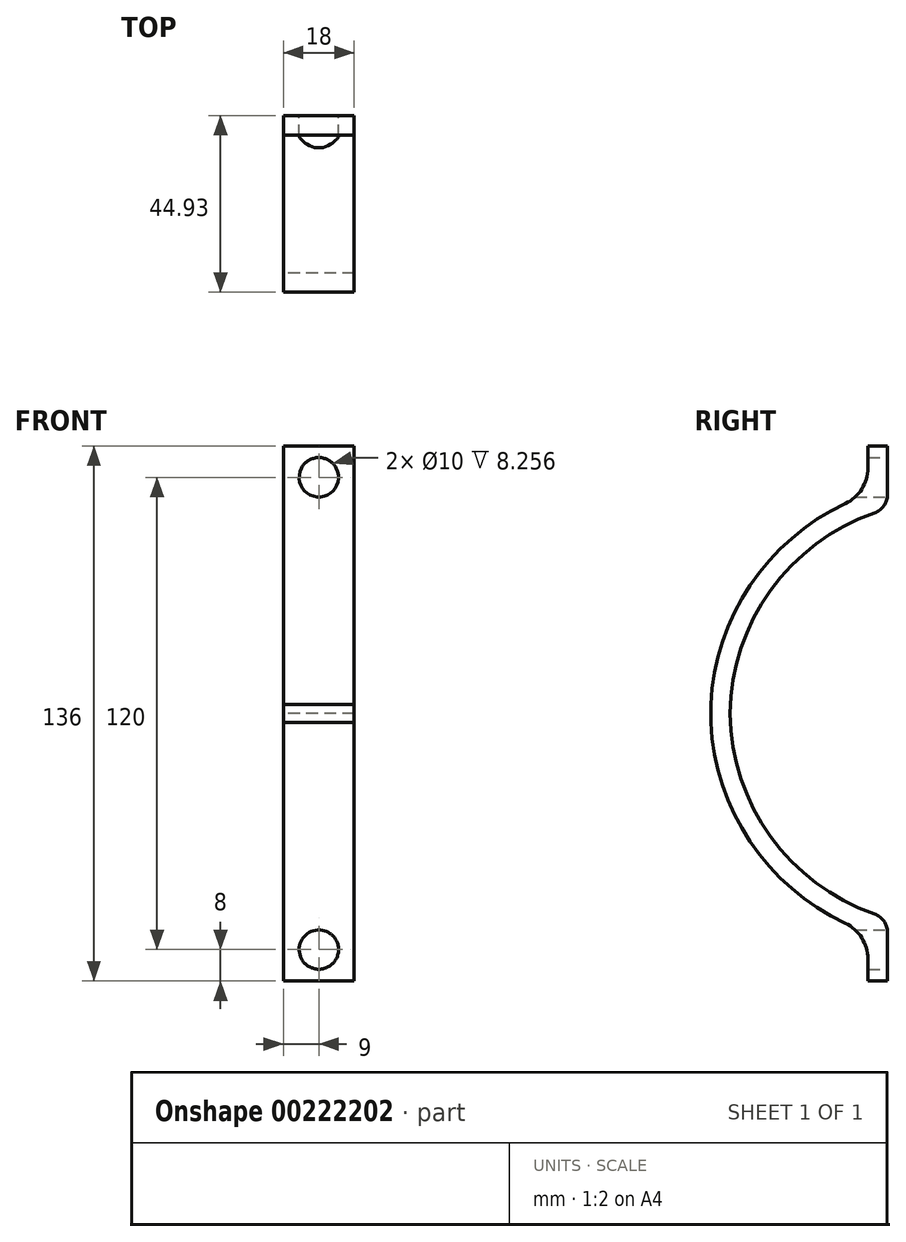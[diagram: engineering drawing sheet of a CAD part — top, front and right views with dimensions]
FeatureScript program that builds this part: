
annotation { "Feature Type Name" : "Feature", "Feature Type Description" : "" }
export const myFeature = defineFeature(function(context is Context, id is Id, definition is map)
    precondition{}
    {
        {
            var Q0;
            Q0=qCreatedBy(makeId("Right.planeOp"),FACE);
            var sketch = newSketch(context, id + "F0", { "sketchPlane" : qUnion([Q0])});
            skLineSegment(sketch, "E0", {"start": v(0, 68) * mm, "end": v(0, 55.67) * mm});
            skLineSegment(sketch, "E1", {"start": v(0, 0) * mm, "end": v(-40, 0) * mm});
            skArc(sketch, "E2", {"start": v(-3.35, 50.95) * mm, "mid": v(-29.72, 31.26) * mm, "end": v(-40, 0) * mm});
            skLineSegment(sketch, "E3", {"start": v(0, 68) * mm, "end": v(-5, 68) * mm});
            skLineSegment(sketch, "E4", {"start": v(-5, 68) * mm, "end": v(-5, 62.37) * mm});
            skArc(sketch, "E5.0", {"start": v(-10.74, 53.33) * mm, "mid": v(-34.92, 32.53) * mm, "end": v(-44.93, 2.26) * mm});
            skLineSegment(sketch, "E6", {"start": v(-44.93, 2.26) * mm, "end": v(-44.93, 0) * mm});
            skLineSegment(sketch, "E7", {"start": v(-44.93, 0) * mm, "end": v(-40, 0) * mm});
            skPoint(sketch, "E8.orphan", {"position": v(0, 57.17) * mm});
            skPoint(sketch, "E9.visualSharp", {"position": v(-5, 55.67) * mm});
            skArc(sketch, "E9.filletArc", {"start": v(-10.74, 53.33) * mm, "mid": v(-6.56, 57.02) * mm, "end": v(-5, 62.37) * mm});
            skPoint(sketch, "E10.visualSharp", {"position": v(0, 52) * mm});
            skArc(sketch, "E10.filletArc", {"start": v(-3.35, 50.95) * mm, "mid": v(-0.92, 52.78) * mm, "end": v(0, 55.67) * mm});
            skLineSegment(sketch, "E11.MirrorCS", {"start": v(-5, -68) * mm, "end": v(-5, -62.37) * mm});
            skArc(sketch, "E12.MirrorCS", {"start": v(-3.35, -50.95) * mm, "mid": v(-0.92, -52.78) * mm, "end": v(0, -55.67) * mm});
            skPoint(sketch, "E13.MirrorP", {"position": v(0, -57.17) * mm});
            skArc(sketch, "E14.MirrorCS", {"start": v(-3.35, -50.95) * mm, "mid": v(-29.72, -31.26) * mm, "end": v(-40, 0) * mm});
            skPoint(sketch, "E15.MirrorP", {"position": v(0, -52) * mm});
            skArc(sketch, "E16.MirrorCS", {"start": v(-10.74, -53.33) * mm, "mid": v(-6.56, -57.02) * mm, "end": v(-5, -62.37) * mm});
            skArc(sketch, "E17.MirrorCS", {"start": v(-10.74, -53.33) * mm, "mid": v(-34.92, -32.53) * mm, "end": v(-44.93, -2.26) * mm});
            skLineSegment(sketch, "E18.MirrorCS", {"start": v(0, -68) * mm, "end": v(0, -55.67) * mm});
            skLineSegment(sketch, "E19.MirrorCS", {"start": v(-44.93, -2.26) * mm, "end": v(-44.93, 0) * mm});
            skLineSegment(sketch, "E20.MirrorCS", {"start": v(0, -68) * mm, "end": v(-5, -68) * mm});
            skPoint(sketch, "E21", {"position": v(-2.74, 60) * mm});
            skPoint(sketch, "E22.MirrorP", {"position": v(-2.74, -60) * mm});
            skSolve(sketch);
        }
        {
            var Q0;
            Q0=makeQuery(id+"F0.imprint","IMPRINT",FACE,{"disambiguationData":[TD([[makeQuery(id+"F0.imprint","IMPRINT",EDGE,{"derivedFrom":sQuery(id+"F0.wireOp",EDGE,"E0")}),-1.0]])]});
            var Q1;
            Q1=makeQuery(id+"F0.imprint","IMPRINT",FACE,{"disambiguationData":[TD([[makeQuery(id+"F0.imprint","IMPRINT",EDGE,{"derivedFrom":sQuery(id+"F0.wireOp",EDGE,"E7")}),-1.0]])]});
            extrude(context, id + "F1", {"entities" : qUnion([Q0, Q1]), "depth" : 18 * mm});
        }
        {
            var Q0;
            Q0=qCreatedBy(makeId("Front.planeOp"),FACE);
            var sketch = newSketch(context, id + "F2", { "sketchPlane" : qUnion([Q0])});
            skPoint(sketch, "E23", {"position": v(9, -60) * mm});
            skPoint(sketch, "E24", {"position": v(9, 60) * mm});
            skSolve(sketch);
        }
        {
            var Q0;
            Q0=sQuery(id+"F2.wireOp",VERTEX,"E24");
            var Q1;
            Q1=sQuery(id+"F2.wireOp",VERTEX,"E23");
            var Q2;
            Q2=makeQuery(id+"F1.opExtrude","SWEPT_BODY",BODY,{"disambiguationData":[OSD([sQuery(id+"F0.wireOp",EDGE,"E0"),sQuery(id+"F0.wireOp",EDGE,"E2"),sQuery(id+"F0.wireOp",EDGE,"E3"),sQuery(id+"F0.wireOp",EDGE,"E4"),sQuery(id+"F0.wireOp",EDGE,"E5.0"),sQuery(id+"F0.wireOp",EDGE,"E6"),sQuery(id+"F0.wireOp",EDGE,"E9.filletArc"),sQuery(id+"F0.wireOp",EDGE,"E10.filletArc"),sQuery(id+"F0.wireOp",EDGE,"E11.MirrorCS"),sQuery(id+"F0.wireOp",EDGE,"E12.MirrorCS"),sQuery(id+"F0.wireOp",EDGE,"E14.MirrorCS"),sQuery(id+"F0.wireOp",EDGE,"E16.MirrorCS"),sQuery(id+"F0.wireOp",EDGE,"E17.MirrorCS"),sQuery(id+"F0.wireOp",EDGE,"E18.MirrorCS"),sQuery(id+"F0.wireOp",EDGE,"E19.MirrorCS"),sQuery(id+"F0.wireOp",EDGE,"E20.MirrorCS")])]});
            hole(context, id + "F3", {"style" : HoleStyle.SIMPLE, "endStyle" : HoleEndStyle.THROUGH, "oppositeDirection" : true, "holeDiameter" : 10 * mm, "startFromSketch" : true, "locations" : qUnion([Q0, Q1]), "scope" : qUnion([Q2]), "isTappedThrough" : true});
        }
    });
